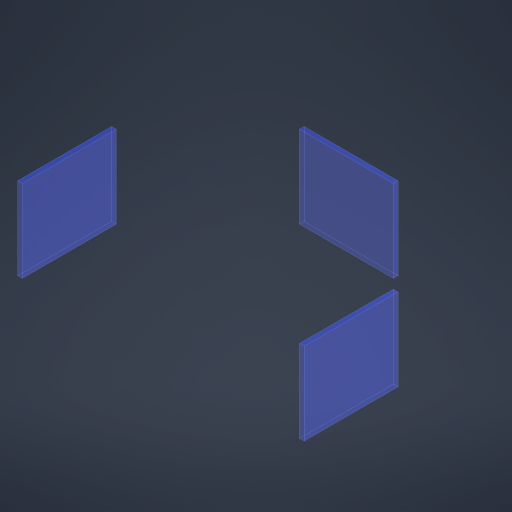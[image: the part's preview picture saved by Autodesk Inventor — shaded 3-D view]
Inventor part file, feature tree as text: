
AUTODESK INVENTOR PART (.ipt)
format: ipt  version: 2023 (Build 270158000, 158)  size: 192,512 bytes
history: native  units: mm
features: other x1, extrude x1, sketch x1
ambient origin geometry x8: Origin, YZ Plane, XZ Plane, XY Plane, X Axis, Y Axis, Z Axis, Center Point
bodies: Body1 (feature_tree)
feature tree (3):
  other  "Těleso1"
  extrude  "Vysunutí1"  Depth=35.0mm TaperAngle=0.0deg
  sketch  "Náčrt2"
